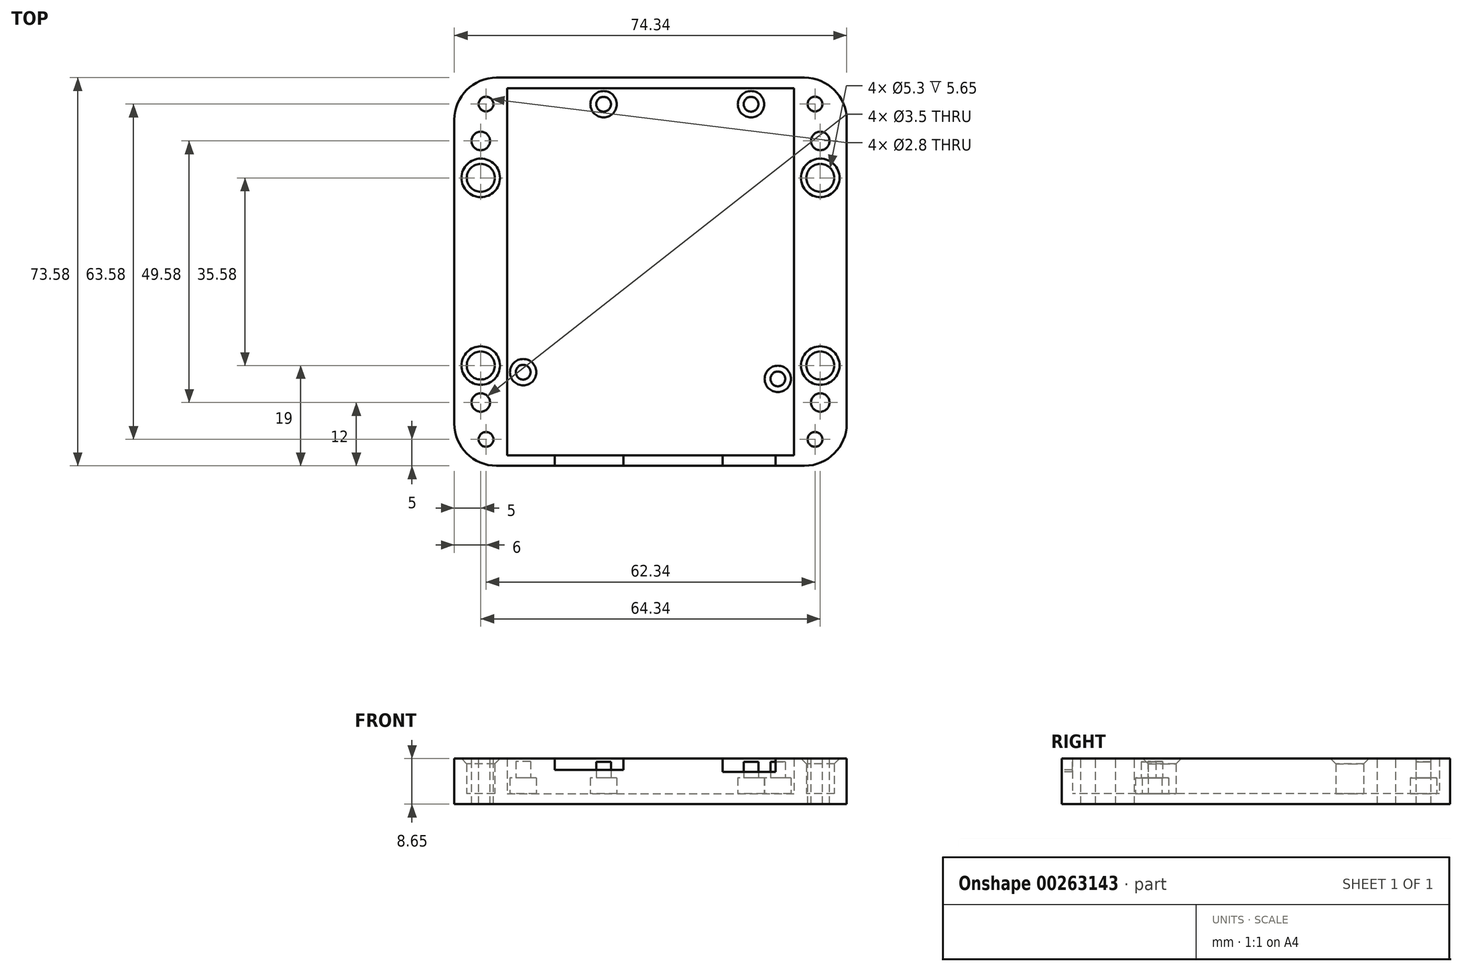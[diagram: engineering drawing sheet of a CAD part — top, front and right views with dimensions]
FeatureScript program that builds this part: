
annotation { "Feature Type Name" : "Feature", "Feature Type Description" : "" }
export const myFeature = defineFeature(function(context is Context, id is Id, definition is map)
    precondition{}
    {
        {
            var Q0;
            Q0=qCreatedBy(makeId("Top.planeOp"),FACE);
            var sketch = newSketch(context, id + "F0", { "sketchPlane" : qUnion([Q0])});
            skLineSegment(sketch, "E0", {"start": v(0, 0) * mm, "end": v(0, 66.04) * mm, "construction": true});
            skLineSegment(sketch, "E1", {"start": v(0, 66.04) * mm, "end": v(12.95, 66.04) * mm, "construction": true});
            skLineSegment(sketch, "E2", {"start": v(12.95, 66.04) * mm, "end": v(15.5, 68.58) * mm, "construction": true});
            skLineSegment(sketch, "E3", {"start": v(15.5, 68.58) * mm, "end": v(48.26, 68.58) * mm, "construction": true});
            skLineSegment(sketch, "E4", {"start": v(48.26, 68.58) * mm, "end": v(50.8, 66.04) * mm, "construction": true});
            skLineSegment(sketch, "E5", {"start": v(50.8, 66.04) * mm, "end": v(53.34, 66.04) * mm, "construction": true});
            skLineSegment(sketch, "E6", {"start": v(53.34, 66.04) * mm, "end": v(53.34, 0) * mm, "construction": true});
            skLineSegment(sketch, "E7", {"start": v(53.34, 0) * mm, "end": v(0, 0) * mm, "construction": true});
            skLineSegment(sketch, "E8", {"start": v(-2.5, 71.08) * mm, "end": v(55.84, 71.08) * mm});
            skLineSegment(sketch, "E9", {"start": v(-2.5, -2.5) * mm, "end": v(55.84, -2.5) * mm});
            skArc(sketch, "E10", {"start": v(63.84, 63.08) * mm, "mid": v(61.5, 68.74) * mm, "end": v(55.84, 71.08) * mm});
            skArc(sketch, "E11", {"start": v(55.84, -2.5) * mm, "mid": v(61.5, -0.16) * mm, "end": v(63.84, 5.5) * mm});
            skLineSegment(sketch, "E12", {"start": v(63.84, 63.08) * mm, "end": v(63.84, 5.5) * mm});
            skArc(sketch, "E13", {"start": v(-10.5, 5.5) * mm, "mid": v(-8.16, -0.16) * mm, "end": v(-2.5, -2.5) * mm});
            skLineSegment(sketch, "E14", {"start": v(-10.5, 63.08) * mm, "end": v(-10.5, 5.5) * mm});
            skArc(sketch, "E15.trimOffspring", {"start": v(-2.5, 71.08) * mm, "mid": v(-8.16, 68.74) * mm, "end": v(-10.5, 63.08) * mm});
            skSolve(sketch);
        }
        {
            var Q0;
            Q0=qSketchRegion(id+"F0",true);
            extrude(context, id + "F1", {"entities" : qUnion([Q0]), "depth" : 2 * mm});
        }
        {
            var Q0;
            Q0=makeQuery(id+"F1.opExtrude","CAP_FACE",FACE,{"disambiguationData":[OSD([sQuery(id+"F0.wireOp",EDGE,"E8"),sQuery(id+"F0.wireOp",EDGE,"E9"),sQuery(id+"F0.wireOp",EDGE,"E10"),sQuery(id+"F0.wireOp",EDGE,"E11"),sQuery(id+"F0.wireOp",EDGE,"E12"),sQuery(id+"F0.wireOp",EDGE,"E13"),sQuery(id+"F0.wireOp",EDGE,"E14"),sQuery(id+"F0.wireOp",EDGE,"E15.trimOffspring")])],"isStart":false});
            var sketch = newSketch(context, id + "F2", { "sketchPlane" : qUnion([Q0])});
            skLineSegment(sketch, "E16", {"start": v(0, 0) * mm, "end": v(53.34, 0) * mm, "construction": true});
            skLineSegment(sketch, "E17", {"start": v(53.34, 0) * mm, "end": v(53.34, 66.04) * mm, "construction": true});
            skLineSegment(sketch, "E18", {"start": v(53.34, 66.04) * mm, "end": v(50.8, 66.04) * mm, "construction": true});
            skLineSegment(sketch, "E19", {"start": v(50.8, 66.04) * mm, "end": v(48.26, 68.58) * mm, "construction": true});
            skLineSegment(sketch, "E20", {"start": v(48.26, 68.58) * mm, "end": v(15.5, 68.58) * mm, "construction": true});
            skLineSegment(sketch, "E21", {"start": v(15.5, 68.58) * mm, "end": v(12.95, 66.04) * mm, "construction": true});
            skLineSegment(sketch, "E22", {"start": v(12.95, 66.04) * mm, "end": v(0, 66.04) * mm, "construction": true});
            skLineSegment(sketch, "E23", {"start": v(0, 66.04) * mm, "end": v(0, 0) * mm, "construction": true});
            skCircle(sketch, "E24", {"center": v(17.78, 66.04) * mm, "radius": 1.59 * mm, "construction": true});
            skCircle(sketch, "E25", {"center": v(45.72, 66.04) * mm, "radius": 1.59 * mm, "construction": true});
            skCircle(sketch, "E26", {"center": v(2.54, 15.24) * mm, "radius": 1.59 * mm, "construction": true});
            skCircle(sketch, "E27", {"center": v(50.8, 13.97) * mm, "radius": 1.59 * mm, "construction": true});
            skCircle(sketch, "E28", {"center": v(17.78, 66.04) * mm, "radius": 2.5 * mm});
            skCircle(sketch, "E29", {"center": v(45.72, 66.04) * mm, "radius": 2.5 * mm});
            skCircle(sketch, "E30", {"center": v(2.54, 15.24) * mm, "radius": 2.5 * mm});
            skCircle(sketch, "E31", {"center": v(50.8, 13.97) * mm, "radius": 2.5 * mm});
            skSolve(sketch);
        }
        {
            var Q0;
            Q0=qSketchRegion(id+"F2",true);
            extrude(context, id + "F3", {"entities" : qUnion([Q0]), "operationType" : NewBodyOperationType.ADD, "depth" : 3 * mm});
        }
        {
            var Q0;
            Q0=makeQuery(id+"F3.opExtrude","CAP_FACE",FACE,{"disambiguationData":[OSD([sQuery(id+"F2.wireOp",EDGE,"E28")])],"isStart":false});
            var sketch = newSketch(context, id + "F4", { "sketchPlane" : qUnion([Q0])});
            skCircle(sketch, "E32", {"center": v(17.78, 66.04) * mm, "radius": 1.4 * mm});
            skSolve(sketch);
        }
        {
            var Q0;
            Q0=qSketchRegion(id+"F4",true);
            extrude(context, id + "F5", {"entities" : qUnion([Q0]), "operationType" : NewBodyOperationType.ADD, "depth" : 3 * mm});
        }
        {
            var Q0;
            Q0=makeQuery(id+"F3.opExtrude","CAP_FACE",FACE,{"disambiguationData":[OSD([sQuery(id+"F2.wireOp",EDGE,"E29")])],"isStart":false});
            var sketch = newSketch(context, id + "F6", { "sketchPlane" : qUnion([Q0])});
            skCircle(sketch, "E33", {"center": v(45.72, 66.04) * mm, "radius": 1.4 * mm});
            skSolve(sketch);
        }
        {
            var Q0;
            Q0=qSketchRegion(id+"F6",true);
            extrude(context, id + "F7", {"entities" : qUnion([Q0]), "operationType" : NewBodyOperationType.ADD, "depth" : 3 * mm});
        }
        {
            var Q0;
            Q0=makeQuery(id+"F3.opExtrude","CAP_FACE",FACE,{"disambiguationData":[OSD([sQuery(id+"F2.wireOp",EDGE,"E30")])],"isStart":false});
            var sketch = newSketch(context, id + "F8", { "sketchPlane" : qUnion([Q0])});
            skCircle(sketch, "E34", {"center": v(2.54, 15.24) * mm, "radius": 1.4 * mm});
            skSolve(sketch);
        }
        {
            var Q0;
            Q0=qSketchRegion(id+"F8",true);
            extrude(context, id + "F9", {"entities" : qUnion([Q0]), "operationType" : NewBodyOperationType.ADD, "depth" : 3.1 * mm});
        }
        {
            var Q0;
            Q0=makeQuery(id+"F3.opExtrude","CAP_FACE",FACE,{"disambiguationData":[OSD([sQuery(id+"F2.wireOp",EDGE,"E31")])],"isStart":false});
            var sketch = newSketch(context, id + "F10", { "sketchPlane" : qUnion([Q0])});
            skCircle(sketch, "E35", {"center": v(50.8, 13.97) * mm, "radius": 1.4 * mm});
            skSolve(sketch);
        }
        {
            var Q0;
            Q0=qSketchRegion(id+"F10",true);
            extrude(context, id + "F11", {"entities" : qUnion([Q0]), "operationType" : NewBodyOperationType.ADD, "depth" : 3 * mm});
        }
        {
            var Q0;
            Q0=makeQuery(id+"F1.opExtrude","CAP_FACE",FACE,{"disambiguationData":[OSD([sQuery(id+"F0.wireOp",EDGE,"E8"),sQuery(id+"F0.wireOp",EDGE,"E9"),sQuery(id+"F0.wireOp",EDGE,"E10"),sQuery(id+"F0.wireOp",EDGE,"E11"),sQuery(id+"F0.wireOp",EDGE,"E12"),sQuery(id+"F0.wireOp",EDGE,"E13"),sQuery(id+"F0.wireOp",EDGE,"E14"),sQuery(id+"F0.wireOp",EDGE,"E15.trimOffspring")])],"isStart":false});
            var sketch = newSketch(context, id + "F12", { "sketchPlane" : qUnion([Q0])});
            skLineSegment(sketch, "E36", {"start": v(-8.5, 55.08) * mm, "end": v(-8.5, 13.5) * mm, "construction": true});
            skLineSegment(sketch, "E37", {"start": v(-10.5, 63.08) * mm, "end": v(-10.5, 5.5) * mm});
            skLineSegment(sketch, "E38", {"start": v(-2.5, -2.5) * mm, "end": v(55.84, -2.5) * mm});
            skLineSegment(sketch, "E39", {"start": v(63.84, 5.5) * mm, "end": v(63.84, 63.08) * mm});
            skLineSegment(sketch, "E40", {"start": v(55.84, 71.08) * mm, "end": v(-2.5, 71.08) * mm});
            skArc(sketch, "E41", {"start": v(-2.5, 71.08) * mm, "mid": v(-8.16, 68.74) * mm, "end": v(-10.5, 63.08) * mm});
            skArc(sketch, "E42", {"start": v(-10.5, 5.5) * mm, "mid": v(-8.16, -0.16) * mm, "end": v(-2.5, -2.5) * mm});
            skArc(sketch, "E43", {"start": v(55.84, -2.5) * mm, "mid": v(61.5, -0.16) * mm, "end": v(63.84, 5.5) * mm});
            skArc(sketch, "E44", {"start": v(63.84, 63.08) * mm, "mid": v(61.5, 68.74) * mm, "end": v(55.84, 71.08) * mm});
            skLineSegment(sketch, "E45", {"start": v(-0.5, 69.08) * mm, "end": v(53.84, 69.08) * mm});
            skLineSegment(sketch, "E46", {"start": v(61.84, 55.08) * mm, "end": v(61.84, 13.5) * mm, "construction": true});
            skLineSegment(sketch, "E47", {"start": v(-0.5, -0.5) * mm, "end": v(53.84, -0.5) * mm});
            skLineSegment(sketch, "E48", {"start": v(-0.5, 69.08) * mm, "end": v(-0.5, -0.5) * mm});
            skLineSegment(sketch, "E49", {"start": v(53.84, 69.08) * mm, "end": v(53.84, -0.5) * mm});
            skCircle(sketch, "E50", {"center": v(-4.5, 66.08) * mm, "radius": 1.4 * mm, "construction": true});
            skCircle(sketch, "E51", {"center": v(-5.5, 59.08) * mm, "radius": 1.75 * mm, "construction": true});
            skLineSegment(sketch, "E52", {"start": v(-8.5, 55.08) * mm, "end": v(-2.5, 55.08) * mm, "construction": true});
            skLineSegment(sketch, "E53.trimOffspring", {"start": v(-2.5, 55.08) * mm, "end": v(-2.5, 13.5) * mm, "construction": true});
            skLineSegment(sketch, "E54", {"start": v(-10.5, 63.08) * mm, "end": v(-0.5, 63.08) * mm, "construction": true});
            skLineSegment(sketch, "E55", {"start": v(55.84, 55.08) * mm, "end": v(61.84, 55.08) * mm, "construction": true});
            skLineSegment(sketch, "E56", {"start": v(63.84, 63.08) * mm, "end": v(53.84, 63.08) * mm, "construction": true});
            skLineSegment(sketch, "E57", {"start": v(-8.5, 13.5) * mm, "end": v(-2.5, 13.5) * mm, "construction": true});
            skPoint(sketch, "E58.end.orphan", {"position": v(-2.5, -0.5) * mm});
            skLineSegment(sketch, "E59", {"start": v(-10.5, 5.5) * mm, "end": v(-0.5, 5.5) * mm, "construction": true});
            skCircle(sketch, "E60", {"center": v(57.84, 66.08) * mm, "radius": 1.4 * mm, "construction": true});
            skCircle(sketch, "E61", {"center": v(58.84, 59.08) * mm, "radius": 1.75 * mm, "construction": true});
            skCircle(sketch, "E62", {"center": v(-5.5, 9.5) * mm, "radius": 1.75 * mm, "construction": true});
            skCircle(sketch, "E63", {"center": v(-4.5, 2.5) * mm, "radius": 1.4 * mm, "construction": true});
            skLineSegment(sketch, "E64", {"start": v(55.84, 13.5) * mm, "end": v(61.84, 13.5) * mm, "construction": true});
            skLineSegment(sketch, "E65", {"start": v(63.84, 5.5) * mm, "end": v(53.84, 5.5) * mm, "construction": true});
            skLineSegment(sketch, "E66", {"start": v(55.84, 55.08) * mm, "end": v(55.84, 13.5) * mm, "construction": true});
            skCircle(sketch, "E67", {"center": v(57.84, 2.5) * mm, "radius": 1.4 * mm, "construction": true});
            skCircle(sketch, "E68", {"center": v(58.84, 9.5) * mm, "radius": 1.75 * mm, "construction": true});
            skCircle(sketch, "E69", {"center": v(-5.5, 52.08) * mm, "radius": 2.65 * mm});
            skCircle(sketch, "E70", {"center": v(-5.5, 16.5) * mm, "radius": 2.65 * mm});
            skCircle(sketch, "E71", {"center": v(58.84, 52.08) * mm, "radius": 2.65 * mm});
            skCircle(sketch, "E72", {"center": v(58.84, 16.5) * mm, "radius": 2.65 * mm});
            skSolve(sketch);
        }
        {
            var Q0;
            Q0=qSketchRegion(id+"F12",true);
            extrude(context, id + "F13", {"entities" : qUnion([Q0]), "operationType" : NewBodyOperationType.ADD, "depth" : 6.65 * mm});
        }
        {
            var Q0;
            Q0=makeQuery(id+"F13.opExtrude","CAP_FACE",FACE,{"disambiguationData":[OSD([sQuery(id+"F12.wireOp",EDGE,"E36"),sQuery(id+"F12.wireOp",EDGE,"E37"),sQuery(id+"F12.wireOp",EDGE,"E38"),sQuery(id+"F12.wireOp",EDGE,"E39"),sQuery(id+"F12.wireOp",EDGE,"E40"),sQuery(id+"F12.wireOp",EDGE,"E41"),sQuery(id+"F12.wireOp",EDGE,"E42"),sQuery(id+"F12.wireOp",EDGE,"E43"),sQuery(id+"F12.wireOp",EDGE,"E44"),sQuery(id+"F12.wireOp",EDGE,"E45"),sQuery(id+"F12.wireOp",EDGE,"E46"),sQuery(id+"F12.wireOp",EDGE,"E47"),sQuery(id+"F12.wireOp",EDGE,"E48"),sQuery(id+"F12.wireOp",EDGE,"E49"),sQuery(id+"F12.wireOp",EDGE,"E52"),sQuery(id+"F12.wireOp",EDGE,"E53.trimOffspring"),sQuery(id+"F12.wireOp",EDGE,"E55"),sQuery(id+"F12.wireOp",EDGE,"E57"),sQuery(id+"F12.wireOp",EDGE,"E64"),sQuery(id+"F12.wireOp",EDGE,"E66")])],"isStart":false});
            var sketch = newSketch(context, id + "F14", { "sketchPlane" : qUnion([Q0])});
            skLineSegment(sketch, "E73", {"start": v(-10.5, 5.5) * mm, "end": v(-0.5, 5.5) * mm, "construction": true});
            skCircle(sketch, "E74", {"center": v(-5.5, 9.5) * mm, "radius": 1.75 * mm});
            skCircle(sketch, "E75", {"center": v(-4.5, 2.5) * mm, "radius": 1.4 * mm});
            skLineSegment(sketch, "E76", {"start": v(63.84, 5.5) * mm, "end": v(53.84, 5.5) * mm, "construction": true});
            skLineSegment(sketch, "E77", {"start": v(-10.5, 63.08) * mm, "end": v(-0.5, 63.08) * mm, "construction": true});
            skLineSegment(sketch, "E78", {"start": v(63.84, 63.08) * mm, "end": v(53.84, 63.08) * mm, "construction": true});
            skCircle(sketch, "E79", {"center": v(-4.5, 66.08) * mm, "radius": 1.4 * mm});
            skCircle(sketch, "E80", {"center": v(-5.5, 59.08) * mm, "radius": 1.75 * mm});
            skCircle(sketch, "E81", {"center": v(57.84, 66.08) * mm, "radius": 1.4 * mm});
            skCircle(sketch, "E82", {"center": v(58.84, 59.08) * mm, "radius": 1.75 * mm});
            skCircle(sketch, "E83", {"center": v(58.84, 9.5) * mm, "radius": 1.75 * mm});
            skCircle(sketch, "E84", {"center": v(57.84, 2.5) * mm, "radius": 1.4 * mm});
            skSolve(sketch);
        }
        {
            var Q0;
            Q0=qSketchRegion(id+"F14",true);
            extrude(context, id + "F15", {"entities" : qUnion([Q0]), "operationType" : NewBodyOperationType.REMOVE, "oppositeDirection" : true, "depth" : 25 * mm});
        }
        {
            var Q0;
            Q0=makeQuery(id+"F13.boolean.opBoolean","MERGE",FACE,{"derivedFrom":[makeQuery(id+"F1.opExtrude","SWEPT_FACE",FACE,{"disambiguationData":[OSD([sQuery(id+"F0.wireOp",EDGE,"E9")])]}),makeQuery(id+"F13.opExtrude","SWEPT_FACE",FACE,{"disambiguationData":[OSD([sQuery(id+"F12.wireOp",EDGE,"E38")])]})]});
            var sketch = newSketch(context, id + "F16", { "sketchPlane" : qUnion([Q0])});
            skLineSegment(sketch, "E85.bottom", {"start": v(8.5, 8.65) * mm, "end": v(21.54, 8.65) * mm});
            skLineSegment(sketch, "E85.top", {"start": v(8.5, 6.52) * mm, "end": v(21.54, 6.52) * mm});
            skLineSegment(sketch, "E85.left", {"start": v(8.5, 8.65) * mm, "end": v(8.5, 6.52) * mm});
            skLineSegment(sketch, "E85.right", {"start": v(21.54, 8.65) * mm, "end": v(21.54, 6.52) * mm});
            skLineSegment(sketch, "E86.bottom", {"start": v(40.34, 8.65) * mm, "end": v(50.34, 8.65) * mm});
            skLineSegment(sketch, "E86.top", {"start": v(40.34, 6.15) * mm, "end": v(50.34, 6.15) * mm});
            skLineSegment(sketch, "E86.left", {"start": v(40.34, 8.65) * mm, "end": v(40.34, 6.15) * mm});
            skLineSegment(sketch, "E86.right", {"start": v(50.34, 8.65) * mm, "end": v(50.34, 6.15) * mm});
            skSolve(sketch);
        }
        {
            var Q0;
            Q0=qSketchRegion(id+"F16",true);
            extrude(context, id + "F17", {"entities" : qUnion([Q0]), "operationType" : NewBodyOperationType.REMOVE, "oppositeDirection" : true, "depth" : 3 * mm});
        }
        {
            var Q0;
            Q0=makeQuery(id+"F13.opExtrude","CAP_EDGE",EDGE,{"disambiguationData":[OSD([sQuery(id+"F12.wireOp",EDGE,"E72")])],"isStart":false});
            var Q1;
            Q1=makeQuery(id+"F13.opExtrude","CAP_EDGE",EDGE,{"disambiguationData":[OSD([sQuery(id+"F12.wireOp",EDGE,"E71")])],"isStart":false});
            var Q2;
            Q2=makeQuery(id+"F13.opExtrude","CAP_EDGE",EDGE,{"disambiguationData":[OSD([sQuery(id+"F12.wireOp",EDGE,"E69")])],"isStart":false});
            var Q3;
            Q3=makeQuery(id+"F13.opExtrude","CAP_EDGE",EDGE,{"disambiguationData":[OSD([sQuery(id+"F12.wireOp",EDGE,"E70")])],"isStart":false});
            chamfer(context, id + "F18", {"entities" : qUnion([Q0, Q1, Q2, Q3]), "width" : 1 * mm, "tangentPropagation" : true});
        }
    });
